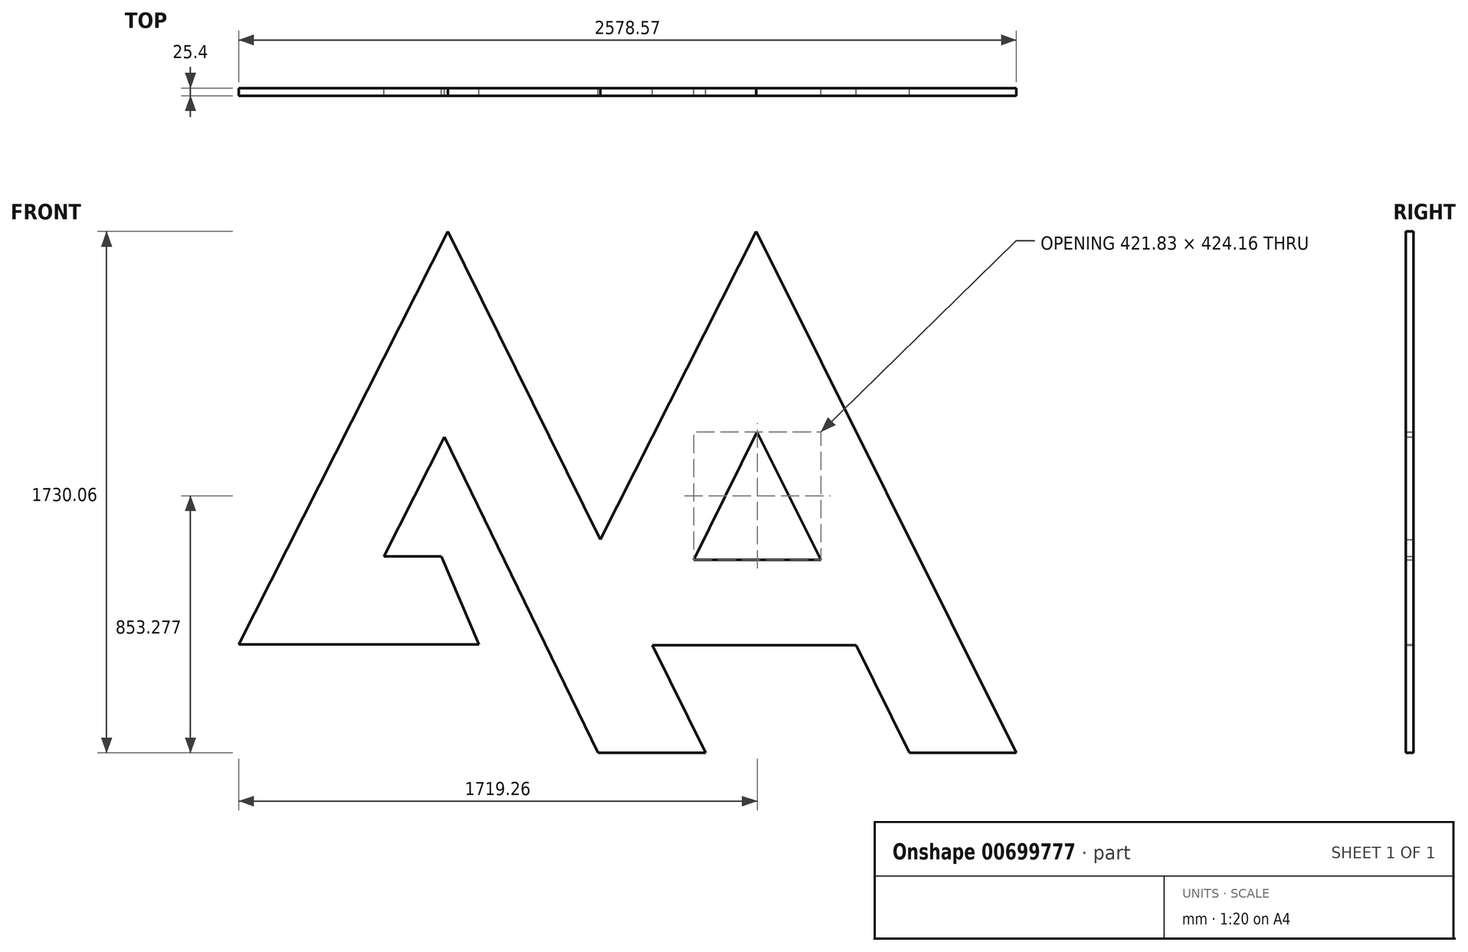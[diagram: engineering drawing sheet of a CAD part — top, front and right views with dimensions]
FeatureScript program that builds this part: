
annotation { "Feature Type Name" : "Feature", "Feature Type Description" : "" }
export const myFeature = defineFeature(function(context is Context, id is Id, definition is map)
    precondition{}
    {
        {
            var Q0;
            Q0=qCreatedBy(makeId("Front.planeOp"),FACE);
            var sketch = newSketch(context, id + "F0", { "sketchPlane" : qUnion([Q0])});
            skLineSegment(sketch, "E0", {"start": v(194.84, 111.14) * mm, "end": v(-498.46, -1259.33) * mm});
            skLineSegment(sketch, "E1", {"start": v(-498.46, -1259.33) * mm, "end": v(297.84, -1259.33) * mm});
            skLineSegment(sketch, "E2", {"start": v(297.84, -1259.33) * mm, "end": v(172.86, -966.52) * mm});
            skLineSegment(sketch, "E3", {"start": v(172.86, -966.52) * mm, "end": v(-17.05, -966.52) * mm});
            skLineSegment(sketch, "E4", {"start": v(-17.05, -966.52) * mm, "end": v(183.17, -570.75) * mm});
            skLineSegment(sketch, "E5", {"start": v(183.17, -570.75) * mm, "end": v(692.54, -1618.92) * mm});
            skLineSegment(sketch, "E6", {"start": v(692.54, -1618.92) * mm, "end": v(1049.86, -1618.92) * mm});
            skLineSegment(sketch, "E7", {"start": v(1049.86, -1618.92) * mm, "end": v(194.84, 111.14) * mm});
            skLineSegment(sketch, "E8", {"start": v(1216.9, 111.14) * mm, "end": v(699.9, -910.81) * mm});
            skLineSegment(sketch, "E9", {"start": v(1216.9, 111.14) * mm, "end": v(2080.1, -1618.92) * mm});
            skLineSegment(sketch, "E10", {"start": v(2080.1, -1618.92) * mm, "end": v(1725.53, -1618.92) * mm});
            skLineSegment(sketch, "E11", {"start": v(1725.53, -1618.92) * mm, "end": v(1549.02, -1261.77) * mm});
            skLineSegment(sketch, "E12", {"start": v(1549.02, -1261.77) * mm, "end": v(873.35, -1261.77) * mm});
            skLineSegment(sketch, "E13", {"start": v(1220.07, -553.56) * mm, "end": v(1431.71, -977.73) * mm});
            skLineSegment(sketch, "E14", {"start": v(1431.71, -977.73) * mm, "end": v(1009.88, -977.73) * mm});
            skLineSegment(sketch, "E15", {"start": v(1009.88, -977.73) * mm, "end": v(1220.07, -553.56) * mm});
            skSolve(sketch);
        }
        {
            var Q0;
            {var subQ0=sQuery(id+"F0.wireOp",EDGE,"E8");Q0=makeQuery(id+"F0.imprint","IMPRINT",FACE,{"disambiguationData":[TD([[makeQuery(id+"F0.imprint","IMPRINT",EDGE,{"derivedFrom":subQ0}),1.0]])]});}
            var Q1;
            {var subQ0=sQuery(id+"F0.wireOp",EDGE,"E0");Q1=makeQuery(id+"F0.imprint","IMPRINT",FACE,{"disambiguationData":[TD([[makeQuery(id+"F0.imprint","IMPRINT",EDGE,{"derivedFrom":subQ0}),1.0]])]});}
            extrude(context, id + "F1", {"entities" : qUnion([Q0, Q1]), "depth" : 25.4 * mm, "offsetDistance" : 25.4 * mm});
        }
    });
